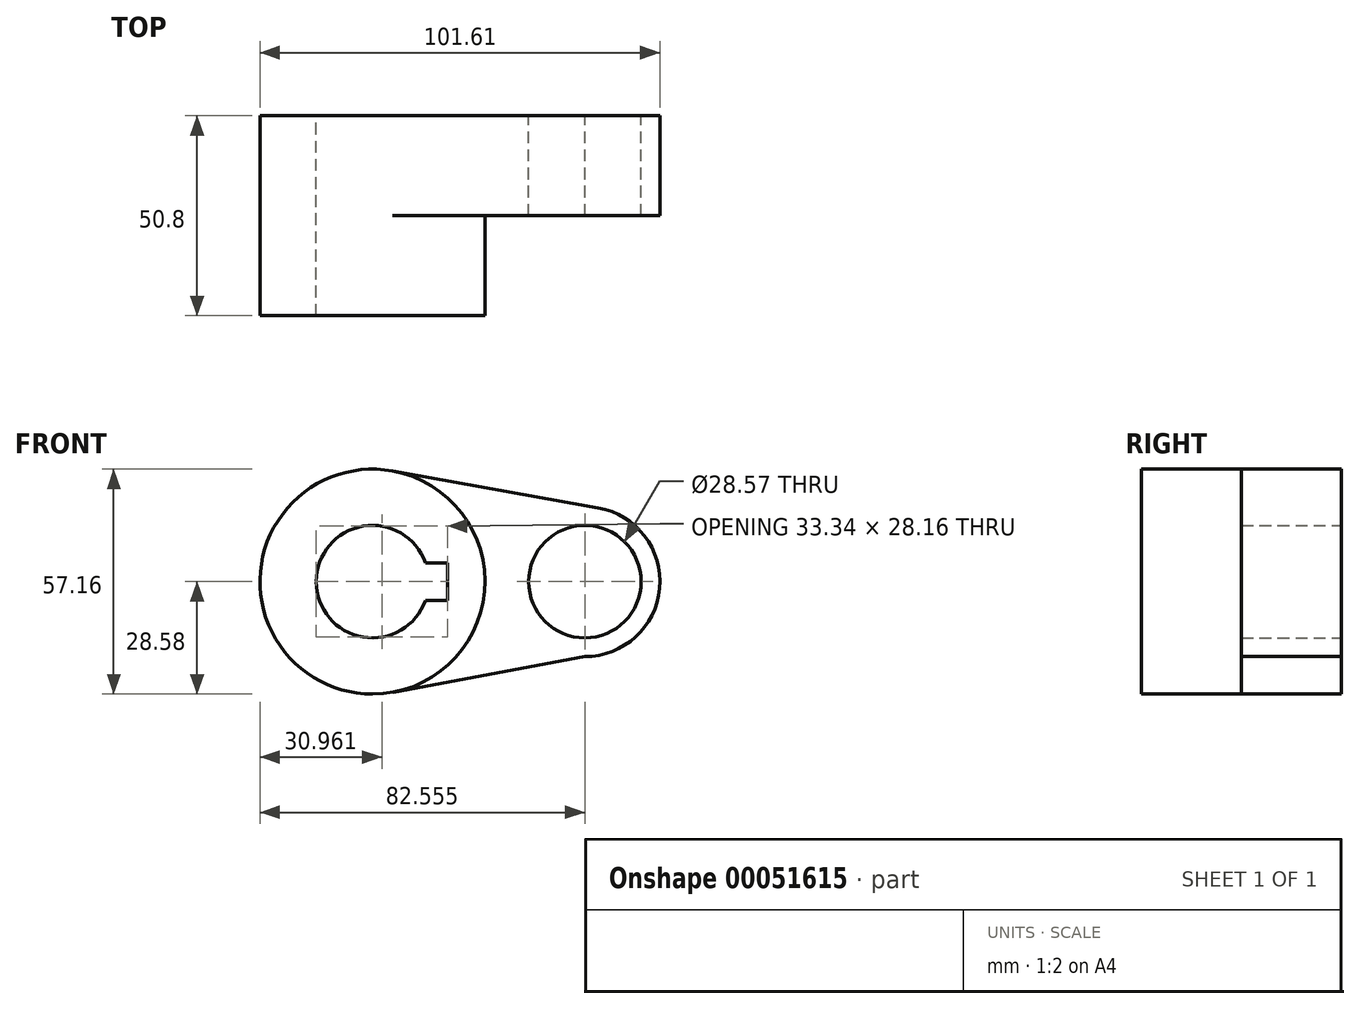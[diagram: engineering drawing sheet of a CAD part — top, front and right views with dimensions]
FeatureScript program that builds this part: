
annotation { "Feature Type Name" : "Feature", "Feature Type Description" : "" }
export const myFeature = defineFeature(function(context is Context, id is Id, definition is map)
    precondition{}
    {
        {
            var Q0;
            Q0=qCreatedBy(makeId("Front.planeOp"),FACE);
            var sketch = newSketch(context, id + "F0", { "sketchPlane" : qUnion([Q0])});
            skCircle(sketch, "E0", {"center": v(0, 0) * mm, "radius": 28.58 * mm});
            skCircle(sketch, "E1", {"center": v(53.97, 0) * mm, "radius": 19.05 * mm});
            skLineSegment(sketch, "E2", {"start": v(5.04, 28.13) * mm, "end": v(57.34, 18.75) * mm});
            skLineSegment(sketch, "E3", {"start": v(5.21, -28.1) * mm, "end": v(53.97, -19.05) * mm});
            skCircle(sketch, "E4", {"center": v(0, 0) * mm, "radius": 14.29 * mm});
            skCircle(sketch, "E5", {"center": v(53.97, 0) * mm, "radius": 14.29 * mm});
            skLineSegment(sketch, "E6.rect.bottom", {"start": v(-19.05, -4.76) * mm, "end": v(19.05, -4.76) * mm});
            skLineSegment(sketch, "E6.rect.top", {"start": v(-19.05, 4.76) * mm, "end": v(19.05, 4.76) * mm});
            skLineSegment(sketch, "E6.rect.left", {"start": v(-19.05, -4.76) * mm, "end": v(-19.05, 4.76) * mm});
            skLineSegment(sketch, "E6.rect.right", {"start": v(19.05, -4.76) * mm, "end": v(19.05, 4.76) * mm});
            skSolve(sketch);
        }
        {
            var Q0;
            {var subQ11=sQuery(id+"F0.wireOp",EDGE,"E6.rect.left");Q0=makeQuery(id+"F0.imprint","IMPRINT",FACE,{"disambiguationData":[TD([[makeQuery(id+"F0.imprint","IMPRINT",EDGE,{"derivedFrom":subQ11}),1.0]])]});}
            var Q1;
            {var subQ5=sQuery(id+"F0.wireOp",EDGE,"E6.rect.left");Q1=makeQuery(id+"F0.imprint","IMPRINT",FACE,{"disambiguationData":[TD([[makeQuery(id+"F0.imprint","IMPRINT",EDGE,{"derivedFrom":subQ5}),-1.0]])]});}
            var Q2;
            {var subQ0=sQuery(id+"F0.wireOp",EDGE,"E2");Q2=makeQuery(id+"F0.imprint","IMPRINT",FACE,{"disambiguationData":[TD([[makeQuery(id+"F0.imprint","IMPRINT",EDGE,{"derivedFrom":subQ0}),-1.0]])]});}
            var Q3;
            Q3=makeQuery(id+"F0.imprint","IMPRINT",FACE,{"disambiguationData":[TD([[makeQuery(id+"F0.imprint","IMPRINT",EDGE,{"derivedFrom":sQuery(id+"F0.wireOp",EDGE,"E5")}),-1.0]])]});
            extrude(context, id + "F1", {"entities" : qUnion([Q0, Q1, Q2, Q3]), "depth" : 25.4 * mm});
        }
        {
            var Q0;
            {var subQ5=sQuery(id+"F0.wireOp",EDGE,"E6.rect.left");Q0=makeQuery(id+"F0.imprint","IMPRINT",FACE,{"disambiguationData":[TD([[makeQuery(id+"F0.imprint","IMPRINT",EDGE,{"derivedFrom":subQ5}),-1.0]])]});}
            var Q1;
            {var subQ11=sQuery(id+"F0.wireOp",EDGE,"E6.rect.left");Q1=makeQuery(id+"F0.imprint","IMPRINT",FACE,{"disambiguationData":[TD([[makeQuery(id+"F0.imprint","IMPRINT",EDGE,{"derivedFrom":subQ11}),1.0]])]});}
            extrude(context, id + "F2", {"entities" : qUnion([Q0, Q1]), "operationType" : NewBodyOperationType.ADD, "depth" : 50.8 * mm});
        }
    });
